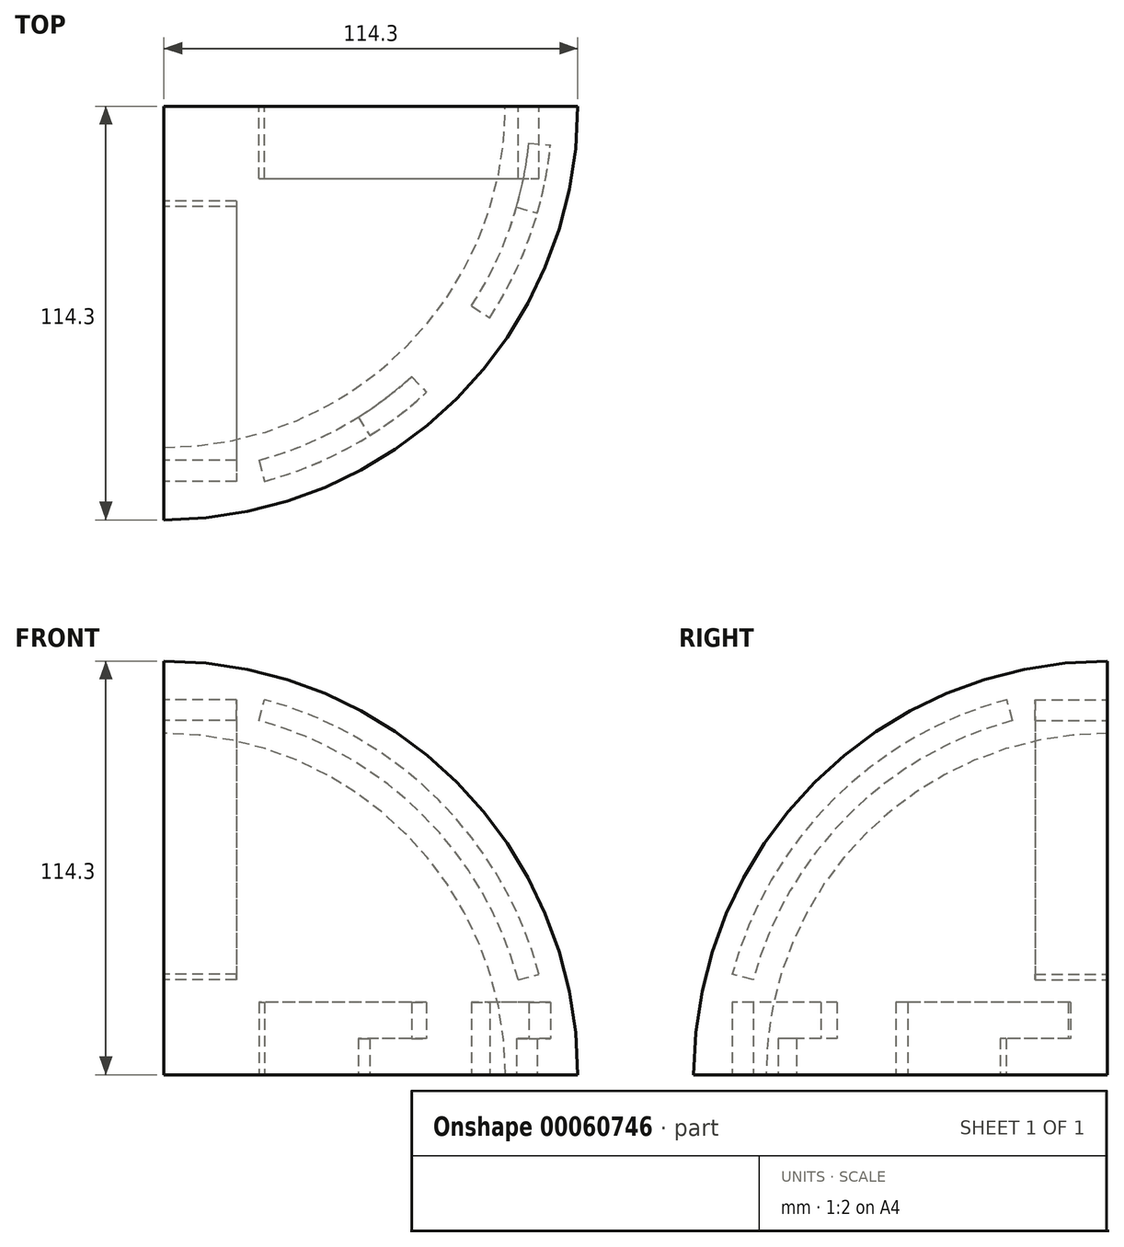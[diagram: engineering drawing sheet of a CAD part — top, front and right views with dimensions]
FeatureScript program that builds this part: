
annotation { "Feature Type Name" : "Feature", "Feature Type Description" : "" }
export const myFeature = defineFeature(function(context is Context, id is Id, definition is map)
    precondition{}
    {
        {
            var Q0;
            Q0=qCreatedBy(makeId("Right.planeOp"),FACE);
            var sketch = newSketch(context, id + "F0", { "sketchPlane" : qUnion([Q0])});
            skArc(sketch, "E0", {"start": v(0, 114.3) * mm, "mid": v(-80.82, 80.82) * mm, "end": v(-114.3, 0) * mm});
            skArc(sketch, "E1", {"start": v(0, 94.3) * mm, "mid": v(-66.68, 66.68) * mm, "end": v(-94.3, 0) * mm});
            skLineSegment(sketch, "E2", {"start": v(0, 94.3) * mm, "end": v(0, 114.3) * mm});
            skLineSegment(sketch, "E3", {"start": v(-94.3, 0) * mm, "end": v(-114.3, 0) * mm});
            skSolve(sketch);
        }
        {
            var Q0;
            Q0=makeQuery(id+"F0.imprint","IMPRINT",FACE,{"disambiguationData":[TD([[makeQuery(id+"F0.imprint","IMPRINT",EDGE,{"derivedFrom":sQuery(id+"F0.wireOp",EDGE,"E0")}),1.0]])]});
            var Q1;
            Q1=sQuery(id+"F0.wireOp",EDGE,"E2");
            revolve(context, id + "F1", {"entities" : qUnion([Q0]), "axis" : qUnion([Q1]), "revolveType" : RevolveType.ONE_DIRECTION, "angle" : 90 * degree});
        }
        {
            var Q0;
            Q0=makeQuery(id+"F1.opRevolve","CAP_FACE",FACE,{"disambiguationData":[OSD([sQuery(id+"F0.wireOp",EDGE,"E0"),sQuery(id+"F0.wireOp",EDGE,"E1"),sQuery(id+"F0.wireOp",EDGE,"E2"),sQuery(id+"F0.wireOp",EDGE,"E3")])],"isStart":false});
            var sketch = newSketch(context, id + "F2", { "sketchPlane" : qUnion([Q0])});
            skArc(sketch, "E4", {"start": v(-27.77, 103.64) * mm, "mid": v(-75.87, 75.87) * mm, "end": v(-103.64, 27.77) * mm});
            skArc(sketch, "E5", {"start": v(-26.22, 97.85) * mm, "mid": v(-71.63, 71.63) * mm, "end": v(-97.85, 26.22) * mm});
            skLineSegment(sketch, "E6", {"start": v(0, 0) * mm, "end": v(-27.77, 103.64) * mm});
            skLineSegment(sketch, "E7", {"start": v(-97.85, 26.22) * mm, "end": v(-103.64, 27.77) * mm});
            skSolve(sketch);
        }
        {
            var Q0;
            Q0=makeQuery(id+"F2.imprint","IMPRINT",FACE,{"disambiguationData":[TD([[makeQuery(id+"F2.imprint","IMPRINT",EDGE,{"derivedFrom":sQuery(id+"F2.wireOp",EDGE,"E4")}),1.0]])]});
            extrude(context, id + "F3", {"entities" : qUnion([Q0]), "operationType" : NewBodyOperationType.REMOVE, "oppositeDirection" : true, "depth" : 20 * mm});
        }
        {
            var Q0;
            Q0=makeQuery(id+"F0.imprint","IMPRINT",FACE,{"disambiguationData":[TD([[makeQuery(id+"F0.imprint","IMPRINT",EDGE,{"derivedFrom":sQuery(id+"F0.wireOp",EDGE,"E0")}),1.0]])]});
            var sketch = newSketch(context, id + "F4", { "sketchPlane" : qUnion([Q0])});
            skArc(sketch, "E8.0", {"start": v(-26.22, 97.85) * mm, "mid": v(-71.63, 71.63) * mm, "end": v(-97.85, 26.22) * mm});
            skArc(sketch, "E9.0", {"start": v(-27.77, 103.64) * mm, "mid": v(-75.87, 75.87) * mm, "end": v(-103.64, 27.77) * mm});
            skLineSegment(sketch, "E10", {"start": v(-26.22, 97.85) * mm, "end": v(-27.77, 103.64) * mm});
            skLineSegment(sketch, "E11", {"start": v(-97.85, 26.22) * mm, "end": v(-103.64, 27.77) * mm});
            skSolve(sketch);
        }
        {
            var Q0;
            Q0=makeQuery(id+"F4.imprint","IMPRINT",FACE,{"disambiguationData":[TD([[makeQuery(id+"F4.imprint","IMPRINT",EDGE,{"derivedFrom":sQuery(id+"F4.wireOp",EDGE,"E8.0")}),-1.0]])]});
            extrude(context, id + "F5", {"entities" : qUnion([Q0]), "operationType" : NewBodyOperationType.REMOVE, "depth" : 20 * mm});
        }
        {
            var Q0;
            Q0=makeQuery(id+"F5.boolean.opBoolean","MERGE",FACE,{"derivedFrom":[makeQuery(id+"F3.boolean.opBoolean","MERGE",FACE,{"derivedFrom":[makeQuery(id+"F1.opRevolve","SWEPT_FACE",FACE,{"disambiguationData":[OSD([sQuery(id+"F0.wireOp",EDGE,"E3")])]}),makeQuery(id+"F3.opExtrude","SWEPT_FACE",FACE,{"disambiguationData":[OSD([sQuery(id+"F2.wireOp",EDGE,"tj54Cu89-9J1S-AJKw-QeEM-ljXHSpR1f2pj")])]})]}),makeQuery(id+"F5.opExtrude","SWEPT_FACE",FACE,{"disambiguationData":[OSD([sQuery(id+"F4.wireOp",EDGE,"EMUQLBOC-9Rso-lLbz-JRUg-i4oPmn0DbPj1")])]})]});
            var sketch = newSketch(context, id + "F6", { "sketchPlane" : qUnion([Q0])});
            skArc(sketch, "E12", {"start": v(97.38, 27.92) * mm, "mid": v(92.18, 42) * mm, "end": v(84.96, 55.17) * mm});
            skArc(sketch, "E13", {"start": v(103.14, 29.58) * mm, "mid": v(97.64, 44.5) * mm, "end": v(89.99, 58.44) * mm});
            skLineSegment(sketch, "E14", {"start": v(26.22, 97.85) * mm, "end": v(27.77, 103.64) * mm});
            skLineSegment(sketch, "E15", {"start": v(53.68, 85.9) * mm, "end": v(56.86, 91) * mm});
            skLineSegment(sketch, "E16", {"start": v(84.96, 55.17) * mm, "end": v(89.99, 58.44) * mm});
            skLineSegment(sketch, "E17", {"start": v(97.38, 27.92) * mm, "end": v(103.14, 29.58) * mm});
            skArc(sketch, "E18.trimOffspring", {"start": v(53.68, 85.9) * mm, "mid": v(40.4, 92.9) * mm, "end": v(26.22, 97.85) * mm});
            skArc(sketch, "E19.trimOffspring", {"start": v(56.86, 91) * mm, "mid": v(42.79, 98.4) * mm, "end": v(27.77, 103.64) * mm});
            skSolve(sketch);
        }
        {
            var Q0;
            Q0=makeQuery(id+"F6.imprint","IMPRINT",FACE,{"disambiguationData":[TD([[makeQuery(id+"F6.imprint","IMPRINT",EDGE,{"derivedFrom":sQuery(id+"F6.wireOp",EDGE,"E14")}),-1.0]])]});
            var Q1;
            Q1=makeQuery(id+"F6.imprint","IMPRINT",FACE,{"disambiguationData":[TD([[makeQuery(id+"F6.imprint","IMPRINT",EDGE,{"derivedFrom":sQuery(id+"F6.wireOp",EDGE,"E12")}),-1.0]])]});
            extrude(context, id + "F7", {"entities" : qUnion([Q0, Q1]), "operationType" : NewBodyOperationType.REMOVE, "oppositeDirection" : true, "depth" : 20 * mm});
        }
        {
            var Q0;
            Q0=makeQuery(id+"F6.imprint","IMPRINT",FACE,{"disambiguationData":[TD([[makeQuery(id+"F6.imprint","IMPRINT",EDGE,{"derivedFrom":sQuery(id+"F6.wireOp",EDGE,"E12")}),1.0]])]});
            cPlane(context, id + "F8", {"entities" : qUnion([Q0]), "cplaneType" : CPlaneType.OFFSET, "offset" : 10 * mm, "oppositeDirection" : true, "width" : 150 * mm, "height" : 150 * mm});
        }
        {
            var Q0;
            Q0=qCreatedBy(id+"F8.planeOp",FACE);
            var sketch = newSketch(context, id + "F9", { "sketchPlane" : qUnion([Q0])});
            skArc(sketch, "E20", {"start": v(100.79, 10.2) * mm, "mid": v(99.48, 19.14) * mm, "end": v(97.38, 27.92) * mm});
            skArc(sketch, "E21", {"start": v(106.76, 10.77) * mm, "mid": v(105.37, 20.25) * mm, "end": v(103.14, 29.58) * mm});
            skLineSegment(sketch, "E22", {"start": v(0, 0) * mm, "end": v(0.33, 0.52) * mm});
            skLineSegment(sketch, "E23", {"start": v(0, 0) * mm, "end": v(0.5, 0.54) * mm});
            skLineSegment(sketch, "E24", {"start": v(0, 0) * mm, "end": v(2.58, 0.74) * mm});
            skLineSegment(sketch, "E25", {"start": v(-5.11, 0) * mm, "end": v(2.58, 0.74) * mm});
            skLineSegment(sketch, "E26.trimOffspring", {"start": v(53.68, 85.9) * mm, "end": v(56.86, 91) * mm});
            skLineSegment(sketch, "E27.trimOffspring", {"start": v(68.44, 74.69) * mm, "end": v(72.5, 79.1) * mm});
            skLineSegment(sketch, "E28.trimOffspring", {"start": v(97.38, 27.92) * mm, "end": v(103.14, 29.58) * mm});
            skLineSegment(sketch, "E29.trimOffspring", {"start": v(100.79, 10.2) * mm, "end": v(106.76, 10.77) * mm});
            skArc(sketch, "E30.trimOffspring", {"start": v(68.44, 74.69) * mm, "mid": v(61.32, 80.64) * mm, "end": v(53.68, 85.9) * mm});
            skArc(sketch, "E31.trimOffspring", {"start": v(72.5, 79.1) * mm, "mid": v(64.95, 85.41) * mm, "end": v(56.86, 91) * mm});
            skSolve(sketch);
        }
        {
            var Q0;
            Q0=qSketchRegion(id+"F9",true);
            extrude(context, id + "F10", {"entities" : qUnion([Q0]), "operationType" : NewBodyOperationType.REMOVE, "oppositeDirection" : true, "depth" : 10 * mm});
        }
    });
